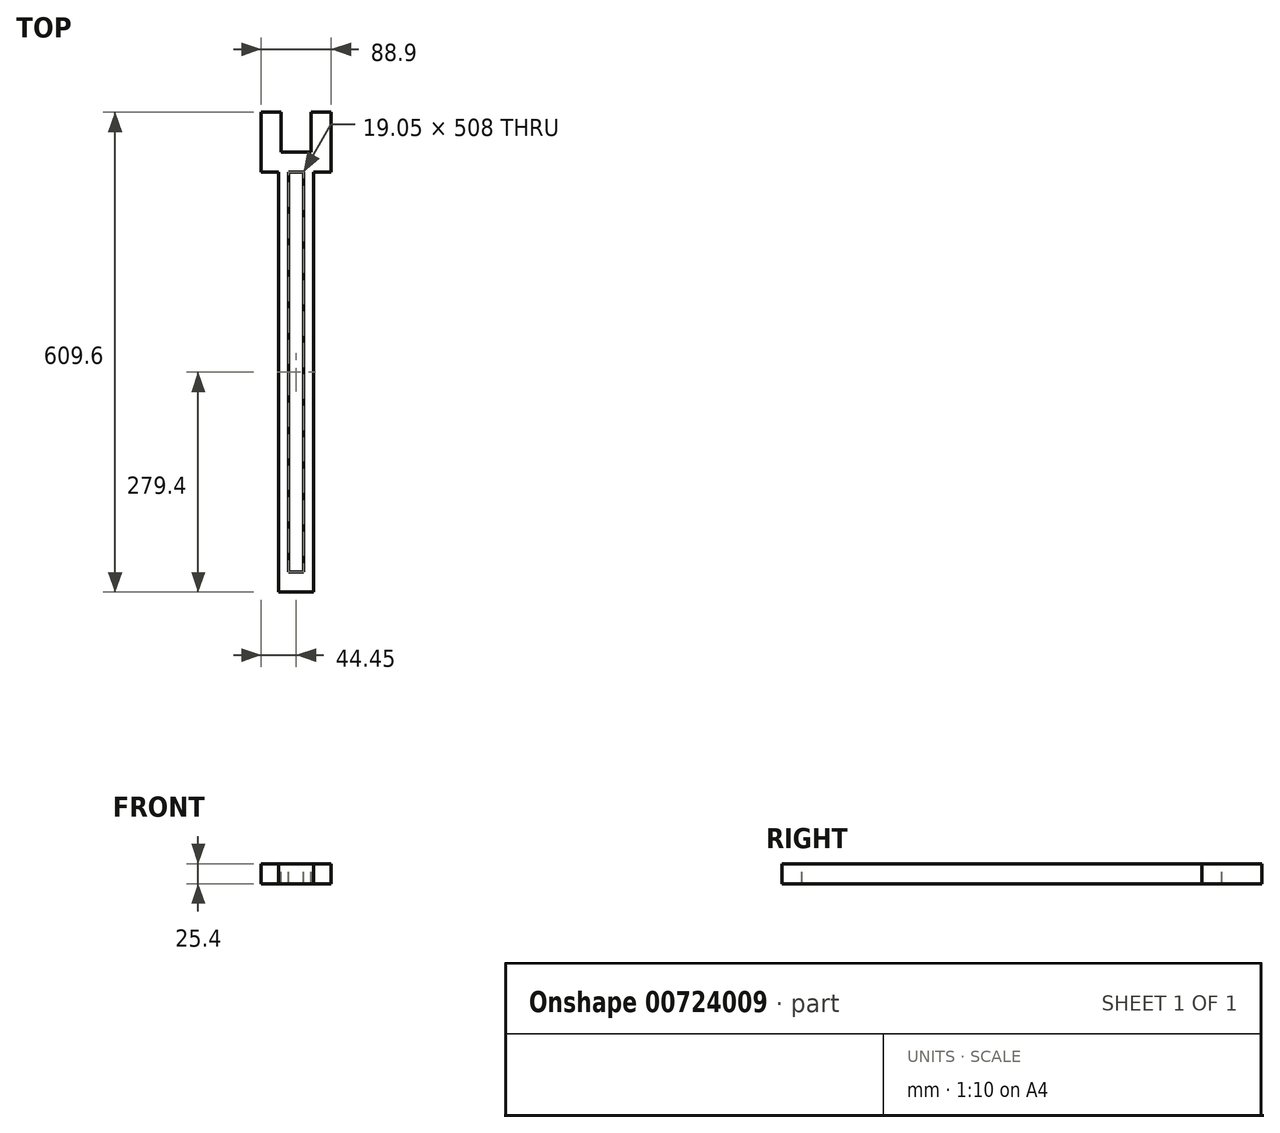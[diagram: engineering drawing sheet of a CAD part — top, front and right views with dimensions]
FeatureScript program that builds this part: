
annotation { "Feature Type Name" : "Feature", "Feature Type Description" : "" }
export const myFeature = defineFeature(function(context is Context, id is Id, definition is map)
    precondition{}
    {
        {
            var Q0;
            Q0=qCreatedBy(makeId("Front.planeOp"),FACE);
            var sketch = newSketch(context, id + "F0", { "sketchPlane" : qUnion([Q0])});
            skLineSegment(sketch, "E0.bottom", {"start": v(22.23, -12.7) * mm, "end": v(-22.23, -12.7) * mm});
            skLineSegment(sketch, "E0.top", {"start": v(22.23, 12.7) * mm, "end": v(-22.23, 12.7) * mm});
            skLineSegment(sketch, "E0.left", {"start": v(22.23, -12.7) * mm, "end": v(22.23, 12.7) * mm});
            skLineSegment(sketch, "E0.right", {"start": v(-22.23, -12.7) * mm, "end": v(-22.23, 12.7) * mm});
            skPoint(sketch, "E0.middle", {"position": v(0, 0) * mm});
            skSolve(sketch);
        }
        {
            var Q0;
            Q0 = qSketchRegion(id + "F0", true);
            extrude(context, id + "F1", {"entities" : qUnion([Q0]), "oppositeDirection" : true, "depth" : 533.4 * mm, "offsetDistance" : 25.4 * mm});
        }
        {
            var Q0;
            Q0=makeQuery(id+"F1.opExtrude","SWEPT_FACE",FACE,{"disambiguationData":[OSD([sQuery(id+"F0.wireOp",EDGE,"E0.top")])]});
            var sketch = newSketch(context, id + "F2", { "sketchPlane" : qUnion([Q0])});
            skLineSegment(sketch, "E1.bottom", {"start": v(9.53, 25.4) * mm, "end": v(-9.52, 25.4) * mm});
            skLineSegment(sketch, "E1.top", {"start": v(9.52, 533.4) * mm, "end": v(-9.53, 533.4) * mm});
            skLineSegment(sketch, "E1.left", {"start": v(9.53, 25.4) * mm, "end": v(9.52, 533.4) * mm});
            skLineSegment(sketch, "E1.right", {"start": v(-9.52, 25.4) * mm, "end": v(-9.53, 533.4) * mm});
            skSolve(sketch);
        }
        {
            var Q0;
            Q0 = qSketchRegion(id + "F2", true);
            extrude(context, id + "F3", {"entities" : qUnion([Q0]), "operationType" : NewBodyOperationType.REMOVE, "oppositeDirection" : true, "depth" : 25.4 * mm, "offsetDistance" : 25.4 * mm});
        }
        {
            var Q0;
            {var subQ0=sQuery(id+"F0.wireOp",EDGE,"E0.bottom");var subQ1=sQuery(id+"F0.wireOp",EDGE,"E0.right");var subQ2=sQuery(id+"F0.wireOp",EDGE,"E0.top");Q0=makeQuery(id+"F3.boolean.opBoolean","SPLIT",FACE,{"disambiguationData":[TD([makeQuery(id+"F1.opExtrude","SWEPT_FACE",FACE,{"disambiguationData":[OSD([subQ1])]})])],"derivedFrom":makeQuery(id+"F1.opExtrude","CAP_FACE",FACE,{"disambiguationData":[OSD([subQ0,subQ2,sQuery(id+"F0.wireOp",EDGE,"E0.left"),subQ1])],"isStart":false})});}
            var sketch = newSketch(context, id + "F4", { "sketchPlane" : qUnion([Q0])});
            skLineSegment(sketch, "E2.bottom", {"start": v(-44.45, -12.7) * mm, "end": v(44.45, -12.7) * mm});
            skLineSegment(sketch, "E2.top", {"start": v(-44.45, 12.7) * mm, "end": v(44.45, 12.7) * mm});
            skLineSegment(sketch, "E2.left", {"start": v(-44.45, -12.7) * mm, "end": v(-44.45, 12.7) * mm});
            skLineSegment(sketch, "E2.right", {"start": v(44.45, -12.7) * mm, "end": v(44.45, 12.7) * mm});
            skSolve(sketch);
        }
        {
            var Q0;
            Q0 = qSketchRegion(id + "F4", true);
            extrude(context, id + "F5", {"entities" : qUnion([Q0]), "operationType" : NewBodyOperationType.ADD, "depth" : 76.2 * mm, "offsetDistance" : 25.4 * mm});
        }
        {
            var Q0;
            Q0=makeQuery(id+"F5.boolean.opBoolean","MERGE",FACE,{"derivedFrom":[makeQuery(id+"F1.opExtrude","SWEPT_FACE",FACE,{"disambiguationData":[OSD([sQuery(id+"F0.wireOp",EDGE,"E0.top")])]}),makeQuery(id+"F5.opExtrude","SWEPT_FACE",FACE,{"disambiguationData":[OSD([sQuery(id+"F4.wireOp",EDGE,"E2.top")])]})]});
            var sketch = newSketch(context, id + "F6", { "sketchPlane" : qUnion([Q0])});
            skLineSegment(sketch, "E3.bottom", {"start": v(19.05, 609.6) * mm, "end": v(-19.05, 609.6) * mm});
            skLineSegment(sketch, "E3.top", {"start": v(19.05, 558.8) * mm, "end": v(-19.05, 558.8) * mm});
            skLineSegment(sketch, "E3.left", {"start": v(19.05, 609.6) * mm, "end": v(19.05, 558.8) * mm});
            skLineSegment(sketch, "E3.right", {"start": v(-19.05, 609.6) * mm, "end": v(-19.05, 558.8) * mm});
            skSolve(sketch);
        }
        {
            var Q0;
            Q0=makeQuery(id+"F6.imprint","IMPRINT",FACE,{"disambiguationData":[TD([[makeQuery(id+"F6.imprint","IMPRINT",EDGE,{"derivedFrom":sQuery(id+"F6.wireOp",EDGE,"E3.bottom")}),1.0]])]});
            extrude(context, id + "F7", {"entities" : qUnion([Q0]), "operationType" : NewBodyOperationType.REMOVE, "oppositeDirection" : true, "depth" : 25.4 * mm, "offsetDistance" : 25.4 * mm});
        }
    });
